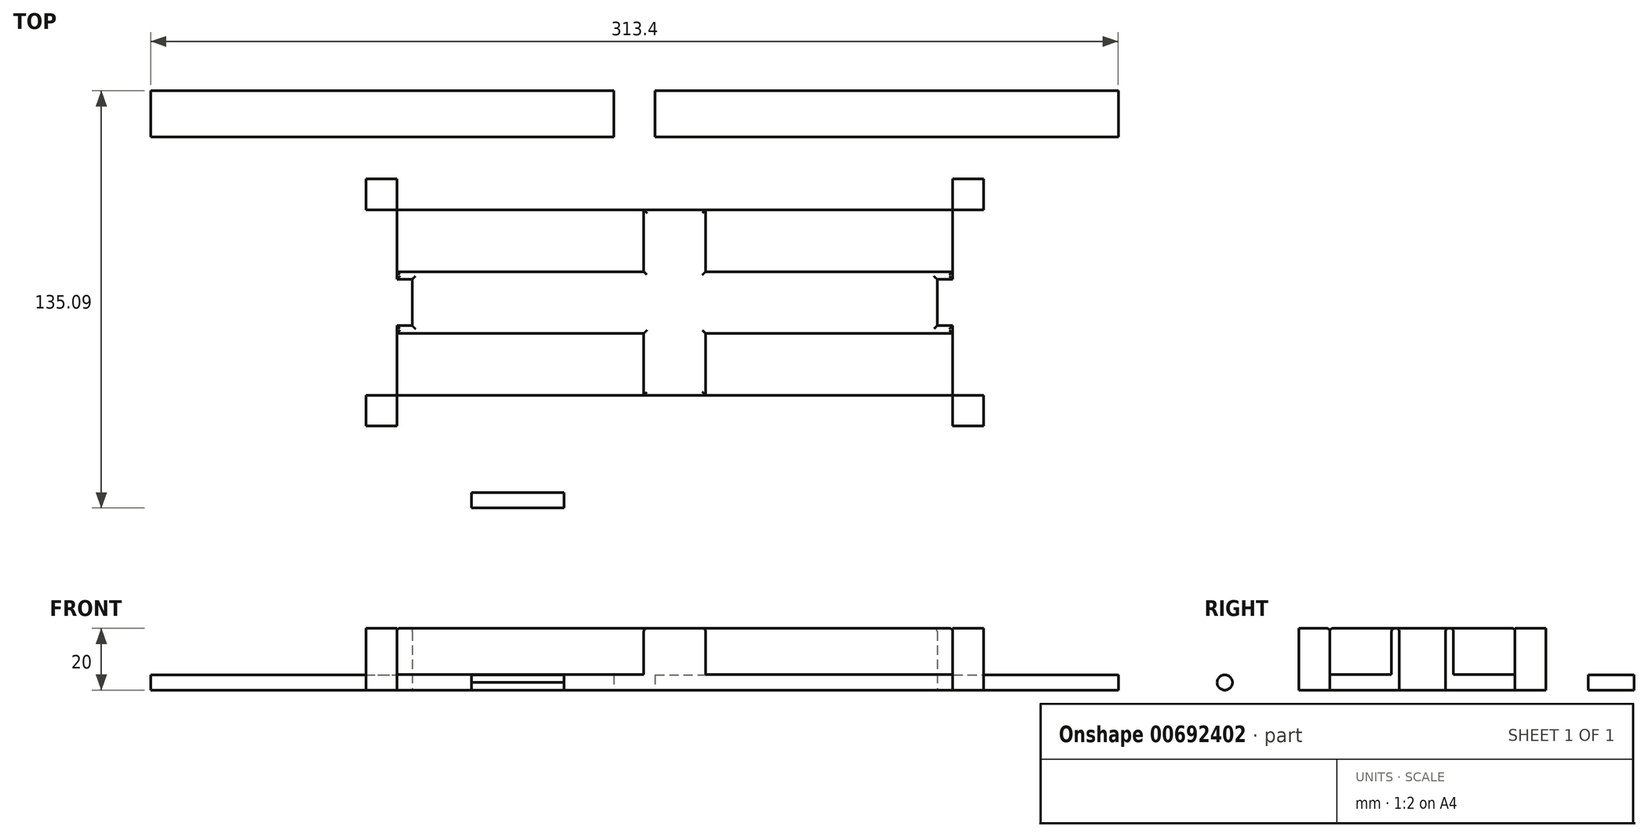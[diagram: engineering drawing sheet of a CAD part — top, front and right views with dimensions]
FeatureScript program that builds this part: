
annotation { "Feature Type Name" : "Feature", "Feature Type Description" : "" }
export const myFeature = defineFeature(function(context is Context, id is Id, definition is map)
    precondition{}
    {
        {
            var Q0;
            Q0=qCreatedBy(makeId("Top.planeOp"),FACE);
            var sketch = newSketch(context, id + "F0", { "sketchPlane" : qUnion([Q0])});
            skLineSegment(sketch, "E0.bottom", {"start": v(100, 40) * mm, "end": v(-100, 40) * mm});
            skLineSegment(sketch, "E0.top", {"start": v(100, -40) * mm, "end": v(-100, -40) * mm});
            skLineSegment(sketch, "E0.left", {"start": v(100, 40) * mm, "end": v(100, -40) * mm});
            skLineSegment(sketch, "E0.right", {"start": v(-100, 40) * mm, "end": v(-100, -40) * mm});
            skPoint(sketch, "E0.middle", {"position": v(0, 0) * mm});
            skLineSegment(sketch, "E1.bottom", {"start": v(-90, 30) * mm, "end": v(-10, 30) * mm});
            skLineSegment(sketch, "E1.top", {"start": v(-90, 10) * mm, "end": v(-10, 10) * mm});
            skLineSegment(sketch, "E1.left", {"start": v(-90, 30) * mm, "end": v(-90, 10) * mm});
            skLineSegment(sketch, "E1.right", {"start": v(-10, 30) * mm, "end": v(-10, 10) * mm});
            skLineSegment(sketch, "E2", {"start": v(-100, 30) * mm, "end": v(100, 30) * mm});
            skLineSegment(sketch, "E3", {"start": v(-90, 40) * mm, "end": v(-90, -40) * mm});
            skLineSegment(sketch, "E4.bottom", {"start": v(-90, -10) * mm, "end": v(-10, -10) * mm});
            skLineSegment(sketch, "E4.top", {"start": v(-90, -30) * mm, "end": v(-10, -30) * mm});
            skLineSegment(sketch, "E4.left", {"start": v(-90, -10) * mm, "end": v(-90, -30) * mm});
            skLineSegment(sketch, "E4.right", {"start": v(-10, -10) * mm, "end": v(-10, -30) * mm});
            skLineSegment(sketch, "E5", {"start": v(-100, -30) * mm, "end": v(100, -30) * mm});
            skLineSegment(sketch, "E6", {"start": v(90, 40) * mm, "end": v(90, -40) * mm});
            skLineSegment(sketch, "E7.bottom", {"start": v(90, -10) * mm, "end": v(10, -10) * mm});
            skLineSegment(sketch, "E7.top", {"start": v(90, -30) * mm, "end": v(10, -30) * mm});
            skLineSegment(sketch, "E7.left", {"start": v(90, -10) * mm, "end": v(90, -30) * mm});
            skLineSegment(sketch, "E7.right", {"start": v(10, -10) * mm, "end": v(10, -30) * mm});
            skLineSegment(sketch, "E8.bottom", {"start": v(90, 10) * mm, "end": v(10, 10) * mm});
            skLineSegment(sketch, "E8.top", {"start": v(90, 30) * mm, "end": v(10, 30) * mm});
            skLineSegment(sketch, "E8.left", {"start": v(90, 10) * mm, "end": v(90, 30) * mm});
            skLineSegment(sketch, "E8.right", {"start": v(10, 10) * mm, "end": v(10, 30) * mm});
            skLineSegment(sketch, "E9.bottom", {"start": v(-90, 7.5) * mm, "end": v(-85, 7.5) * mm});
            skLineSegment(sketch, "E9.top", {"start": v(-90, -7.5) * mm, "end": v(-85, -7.5) * mm});
            skLineSegment(sketch, "E9.left", {"start": v(-90, 7.5) * mm, "end": v(-90, -7.5) * mm});
            skLineSegment(sketch, "E9.right", {"start": v(-85, 7.5) * mm, "end": v(-85, -7.5) * mm});
            skLineSegment(sketch, "E10.bottom", {"start": v(85, 7.5) * mm, "end": v(90, 7.5) * mm});
            skLineSegment(sketch, "E10.top", {"start": v(85, -7.5) * mm, "end": v(90, -7.5) * mm});
            skLineSegment(sketch, "E10.left", {"start": v(85, 7.5) * mm, "end": v(85, -7.5) * mm});
            skLineSegment(sketch, "E10.right", {"start": v(90, 7.5) * mm, "end": v(90, -7.5) * mm});
            skSolve(sketch);
        }
        {
            var Q0;
            {var subQ4=sQuery(id+"F0.wireOp",EDGE,"E1.top");Q0=makeQuery(id+"F0.imprint","IMPRINT",FACE,{"disambiguationData":[TD([[makeQuery(id+"F0.imprint","IMPRINT",EDGE,{"derivedFrom":subQ4}),-1.0]])]});}
            var Q1;
            {var subQ7=sQuery(id+"F0.wireOp",EDGE,"E4.left");Q1=makeQuery(id+"F0.imprint","IMPRINT",FACE,{"disambiguationData":[TD([[makeQuery(id+"F0.imprint","IMPRINT",EDGE,{"derivedFrom":subQ7}),-1.0]])]});}
            var Q2;
            {var subQ0=sQuery(id+"F0.wireOp",EDGE,"E0.right");var subQ1=sQuery(id+"F0.wireOp",EDGE,"E0.top");var subQ2=makeQuery(id+"F0.imprint","INTERSECT",VERTEX,{"derivedFrom":[subQ1,subQ0]});Q2=makeQuery(id+"F0.imprint","IMPRINT",FACE,{"disambiguationData":[TD([[makeQuery(id+"F0.imprint","IMPRINT",EDGE,{"disambiguationData":[TD([[subQ2,1.0]])],"derivedFrom":subQ1}),-1.0]])]});}
            var Q3;
            {var subQ2=sQuery(id+"F0.wireOp",EDGE,"E7.top");Q3=makeQuery(id+"F0.imprint","IMPRINT",FACE,{"disambiguationData":[TD([[makeQuery(id+"F0.imprint","IMPRINT",EDGE,{"derivedFrom":subQ2}),1.0]])]});}
            var Q4;
            {var subQ0=sQuery(id+"F0.wireOp",EDGE,"E0.right");var subQ1=sQuery(id+"F0.wireOp",EDGE,"E0.bottom");var subQ2=makeQuery(id+"F0.imprint","INTERSECT",VERTEX,{"derivedFrom":[subQ1,subQ0]});Q4=makeQuery(id+"F0.imprint","IMPRINT",FACE,{"disambiguationData":[TD([[makeQuery(id+"F0.imprint","IMPRINT",EDGE,{"disambiguationData":[TD([[subQ2,1.0]])],"derivedFrom":subQ1}),1.0]])]});}
            var Q5;
            {var subQ7=sQuery(id+"F0.wireOp",EDGE,"E8.top");Q5=makeQuery(id+"F0.imprint","IMPRINT",FACE,{"disambiguationData":[TD([[makeQuery(id+"F0.imprint","IMPRINT",EDGE,{"derivedFrom":subQ7}),-1.0]])]});}
            var Q6;
            {var subQ0=sQuery(id+"F0.wireOp",EDGE,"E0.left");var subQ1=sQuery(id+"F0.wireOp",EDGE,"E0.bottom");var subQ2=makeQuery(id+"F0.imprint","INTERSECT",VERTEX,{"derivedFrom":[subQ1,subQ0]});Q6=makeQuery(id+"F0.imprint","IMPRINT",FACE,{"disambiguationData":[TD([[makeQuery(id+"F0.imprint","IMPRINT",EDGE,{"disambiguationData":[TD([[subQ2,-1.0]])],"derivedFrom":subQ1}),1.0]])]});}
            var Q7;
            {var subQ0=sQuery(id+"F0.wireOp",EDGE,"E7.left");Q7=makeQuery(id+"F0.imprint","IMPRINT",FACE,{"disambiguationData":[TD([[makeQuery(id+"F0.imprint","IMPRINT",EDGE,{"derivedFrom":subQ0}),1.0]])]});}
            var Q8;
            {var subQ0=sQuery(id+"F0.wireOp",EDGE,"E0.left");var subQ1=sQuery(id+"F0.wireOp",EDGE,"E0.top");var subQ2=makeQuery(id+"F0.imprint","INTERSECT",VERTEX,{"derivedFrom":[subQ1,subQ0]});Q8=makeQuery(id+"F0.imprint","IMPRINT",FACE,{"disambiguationData":[TD([[makeQuery(id+"F0.imprint","IMPRINT",EDGE,{"disambiguationData":[TD([[subQ2,-1.0]])],"derivedFrom":subQ1}),-1.0]])]});}
            extrude(context, id + "F1", {"entities" : qUnion([Q0, Q1, Q2, Q3, Q4, Q5, Q6, Q7, Q8]), "depth" : 20 * mm, "offsetDistance" : 25.4 * mm});
        }
        {
            var Q0;
            {var subQ0=sQuery(id+"F0.wireOp",EDGE,"E1.top");Q0=makeQuery(id+"F0.imprint","IMPRINT",FACE,{"disambiguationData":[TD([[makeQuery(id+"F0.imprint","IMPRINT",EDGE,{"derivedFrom":subQ0}),1.0]])]});}
            extrude(context, id + "F2", {"entities" : qUnion([Q0]), "operationType" : NewBodyOperationType.ADD, "depth" : 5 * mm, "offsetDistance" : 25.4 * mm});
        }
        {
            var Q0;
            Q0=makeQuery(id+"F0.imprint","IMPRINT",FACE,{"disambiguationData":[TD([[makeQuery(id+"F0.imprint","IMPRINT",EDGE,{"derivedFrom":sQuery(id+"F0.wireOp",EDGE,"E4.bottom")}),-1.0]])]});
            extrude(context, id + "F3", {"entities" : qUnion([Q0]), "operationType" : NewBodyOperationType.ADD, "depth" : 5 * mm, "offsetDistance" : 25.4 * mm});
        }
        {
            var Q0;
            Q0=makeQuery(id+"F0.imprint","IMPRINT",FACE,{"disambiguationData":[TD([[makeQuery(id+"F0.imprint","IMPRINT",EDGE,{"derivedFrom":sQuery(id+"F0.wireOp",EDGE,"E8.bottom")}),-1.0]])]});
            extrude(context, id + "F4", {"entities" : qUnion([Q0]), "operationType" : NewBodyOperationType.ADD, "depth" : 5 * mm, "offsetDistance" : 25.4 * mm});
        }
        {
            var Q0;
            Q0=makeQuery(id+"F0.imprint","IMPRINT",FACE,{"disambiguationData":[TD([[makeQuery(id+"F0.imprint","IMPRINT",EDGE,{"derivedFrom":sQuery(id+"F0.wireOp",EDGE,"E7.bottom")}),1.0]])]});
            extrude(context, id + "F5", {"entities" : qUnion([Q0]), "operationType" : NewBodyOperationType.ADD, "depth" : 5 * mm, "offsetDistance" : 25.4 * mm});
        }
        {
            var Q0;
            Q0=qCreatedBy(makeId("Top.planeOp"),FACE);
            var sketch = newSketch(context, id + "F6", { "sketchPlane" : qUnion([Q0])});
            skLineSegment(sketch, "E11.bottom", {"start": v(-169.73, 68.57) * mm, "end": v(-19.73, 68.57) * mm});
            skLineSegment(sketch, "E11.top", {"start": v(-169.73, 53.67) * mm, "end": v(-19.73, 53.67) * mm});
            skLineSegment(sketch, "E11.left", {"start": v(-169.73, 68.57) * mm, "end": v(-169.73, 53.67) * mm});
            skLineSegment(sketch, "E11.right", {"start": v(-19.73, 68.57) * mm, "end": v(-19.73, 53.67) * mm});
            skPoint(sketch, "E12.firstSnap0", {"position": v(-94.73, 68.57) * mm});
            skLineSegment(sketch, "E12.bottom", {"start": v(-6.33, 68.57) * mm, "end": v(143.67, 68.57) * mm});
            skLineSegment(sketch, "E12.top", {"start": v(-6.33, 53.67) * mm, "end": v(143.67, 53.67) * mm});
            skLineSegment(sketch, "E12.left", {"start": v(-6.33, 68.57) * mm, "end": v(-6.33, 53.67) * mm});
            skLineSegment(sketch, "E12.right", {"start": v(143.67, 68.57) * mm, "end": v(143.67, 53.67) * mm});
            skLineSegment(sketch, "E13.bottom", {"start": v(-65.84, -61.52) * mm, "end": v(-35.84, -61.52) * mm});
            skLineSegment(sketch, "E13.top", {"start": v(-65.84, -66.52) * mm, "end": v(-35.84, -66.52) * mm});
            skLineSegment(sketch, "E13.left", {"start": v(-65.84, -61.52) * mm, "end": v(-65.84, -66.52) * mm});
            skLineSegment(sketch, "E13.right", {"start": v(-35.84, -61.52) * mm, "end": v(-35.84, -66.52) * mm});
            skSolve(sketch);
        }
        {
            var Q0;
            Q0 = qSketchRegion(id + "F6", true);
            var Q1;
            Q1=makeQuery(id+"F6.imprint","IMPRINT",FACE,{"disambiguationData":[TD([[makeQuery(id+"F6.imprint","IMPRINT",EDGE,{"derivedFrom":sQuery(id+"F6.wireOp",EDGE,"E11.bottom")}),-1.0]])]});
            extrude(context, id + "F7", {"entities" : qUnion([Q0, Q1]), "depth" : 4.9 * mm, "offsetDistance" : 25.4 * mm});
        }
        {
            var Q0;
            Q0=makeQuery(id+"F1.opExtrude","CAP_EDGE",EDGE,{"disambiguationData":[OSD([sQuery(id+"F0.wireOp",EDGE,"E9.left")])],"isStart":false});
            var Q1;
            Q1=makeQuery(id+"F1.opExtrude","CAP_EDGE",EDGE,{"disambiguationData":[OSD([sQuery(id+"F0.wireOp",EDGE,"E9.right")])],"isStart":false});
            var Q2;
            Q2=makeQuery(id+"F1.opExtrude","CAP_EDGE",EDGE,{"disambiguationData":[OSD([sQuery(id+"F0.wireOp",EDGE,"E9.bottom")])],"isStart":false});
            var Q3;
            Q3=makeQuery(id+"F1.opExtrude","CAP_EDGE",EDGE,{"disambiguationData":[OSD([sQuery(id+"F0.wireOp",EDGE,"E9.top")])],"isStart":false});
            var Q4;
            Q4=makeQuery(id+"F1.opExtrude","CAP_EDGE",EDGE,{"disambiguationData":[OSD([sQuery(id+"F0.wireOp",EDGE,"E10.left")])],"isStart":false});
            var Q5;
            Q5=makeQuery(id+"F1.opExtrude","CAP_EDGE",EDGE,{"disambiguationData":[OSD([sQuery(id+"F0.wireOp",EDGE,"E10.bottom")])],"isStart":false});
            var Q6;
            Q6=makeQuery(id+"F1.opExtrude","CAP_EDGE",EDGE,{"disambiguationData":[OSD([sQuery(id+"F0.wireOp",EDGE,"E10.right")])],"isStart":false});
            var Q7;
            Q7=makeQuery(id+"F1.opExtrude","CAP_EDGE",EDGE,{"disambiguationData":[OSD([sQuery(id+"F0.wireOp",EDGE,"E10.top")])],"isStart":false});
            var Q8;
            Q8=makeQuery(id+"F1.opExtrude","CAP_EDGE",EDGE,{"disambiguationData":[OSD([sQuery(id+"F0.wireOp",EDGE,"E4.bottom")])],"isStart":false});
            var Q9;
            Q9=makeQuery(id+"F1.opExtrude","CAP_EDGE",EDGE,{"disambiguationData":[OSD([sQuery(id+"F0.wireOp",EDGE,"E4.left")])],"isStart":false});
            var Q10;
            Q10=makeQuery(id+"F1.opExtrude","CAP_EDGE",EDGE,{"disambiguationData":[OSD([sQuery(id+"F0.wireOp",EDGE,"E5")])],"isStart":false});
            var Q11;
            Q11=makeQuery(id+"F1.opExtrude","CAP_EDGE",EDGE,{"disambiguationData":[OSD([sQuery(id+"F0.wireOp",EDGE,"E4.right")])],"isStart":false});
            var Q12;
            Q12=makeQuery(id+"F1.opExtrude","CAP_EDGE",EDGE,{"disambiguationData":[OSD([sQuery(id+"F0.wireOp",EDGE,"E7.bottom")])],"isStart":false});
            var Q13;
            Q13=makeQuery(id+"F1.opExtrude","CAP_EDGE",EDGE,{"disambiguationData":[OSD([sQuery(id+"F0.wireOp",EDGE,"E7.right")])],"isStart":false});
            var Q14;
            Q14=makeQuery(id+"F1.opExtrude","CAP_EDGE",EDGE,{"disambiguationData":[OSD([sQuery(id+"F0.wireOp",EDGE,"E7.top")])],"isStart":false});
            var Q15;
            Q15=makeQuery(id+"F1.opExtrude","CAP_EDGE",EDGE,{"disambiguationData":[OSD([sQuery(id+"F0.wireOp",EDGE,"E7.left")])],"isStart":false});
            var Q16;
            Q16=makeQuery(id+"F1.opExtrude","CAP_FACE",FACE,{"disambiguationData":[OSD([sQuery(id+"F0.wireOp",EDGE,"E0.bottom"),sQuery(id+"F0.wireOp",EDGE,"E0.top"),sQuery(id+"F0.wireOp",EDGE,"E0.left"),sQuery(id+"F0.wireOp",EDGE,"E0.right"),sQuery(id+"F0.wireOp",EDGE,"E1.top"),sQuery(id+"F0.wireOp",EDGE,"E1.right"),sQuery(id+"F0.wireOp",EDGE,"E2"),sQuery(id+"F0.wireOp",EDGE,"E3"),sQuery(id+"F0.wireOp",EDGE,"E4.bottom"),sQuery(id+"F0.wireOp",EDGE,"E4.left"),sQuery(id+"F0.wireOp",EDGE,"E4.right"),sQuery(id+"F0.wireOp",EDGE,"E5"),sQuery(id+"F0.wireOp",EDGE,"E7.bottom"),sQuery(id+"F0.wireOp",EDGE,"E7.top"),sQuery(id+"F0.wireOp",EDGE,"E7.left"),sQuery(id+"F0.wireOp",EDGE,"E7.right"),sQuery(id+"F0.wireOp",EDGE,"E8.bottom"),sQuery(id+"F0.wireOp",EDGE,"E8.top"),sQuery(id+"F0.wireOp",EDGE,"E8.left"),sQuery(id+"F0.wireOp",EDGE,"E8.right"),sQuery(id+"F0.wireOp",EDGE,"E9.bottom"),sQuery(id+"F0.wireOp",EDGE,"E9.top"),sQuery(id+"F0.wireOp",EDGE,"E9.left"),sQuery(id+"F0.wireOp",EDGE,"E9.right"),sQuery(id+"F0.wireOp",EDGE,"E10.bottom"),sQuery(id+"F0.wireOp",EDGE,"E10.top"),sQuery(id+"F0.wireOp",EDGE,"E10.left"),sQuery(id+"F0.wireOp",EDGE,"E10.right")])],"isStart":false});
            fillet(context, id + "F8", {"entities" : qUnion([Q0, Q1, Q2, Q3, Q4, Q5, Q6, Q7, Q8, Q9, Q10, Q11, Q12, Q13, Q14, Q15, Q16]), "radius" : 1 * mm, "tangentPropagation" : true, "allowEdgeOverflow" : false});
        }
        {
            var Q0;
            Q0=makeQuery(id+"F7.opExtrude","CAP_EDGE",EDGE,{"disambiguationData":[OSD([sQuery(id+"F6.wireOp",EDGE,"E13.top")])],"isStart":false});
            var Q1;
            Q1=makeQuery(id+"F7.opExtrude","CAP_EDGE",EDGE,{"disambiguationData":[OSD([sQuery(id+"F6.wireOp",EDGE,"E13.bottom")])],"isStart":false});
            var Q2;
            Q2=makeQuery(id+"F7.opExtrude","CAP_EDGE",EDGE,{"disambiguationData":[OSD([sQuery(id+"F6.wireOp",EDGE,"E13.top")])],"isStart":true});
            var Q3;
            Q3=makeQuery(id+"F7.opExtrude","CAP_EDGE",EDGE,{"disambiguationData":[OSD([sQuery(id+"F6.wireOp",EDGE,"E13.bottom")])],"isStart":true});
            fillet(context, id + "F9", {"entities" : qUnion([Q0, Q1, Q2, Q3]), "radius" : 2.5 * mm, "tangentPropagation" : true, "allowEdgeOverflow" : false});
        }
    });
